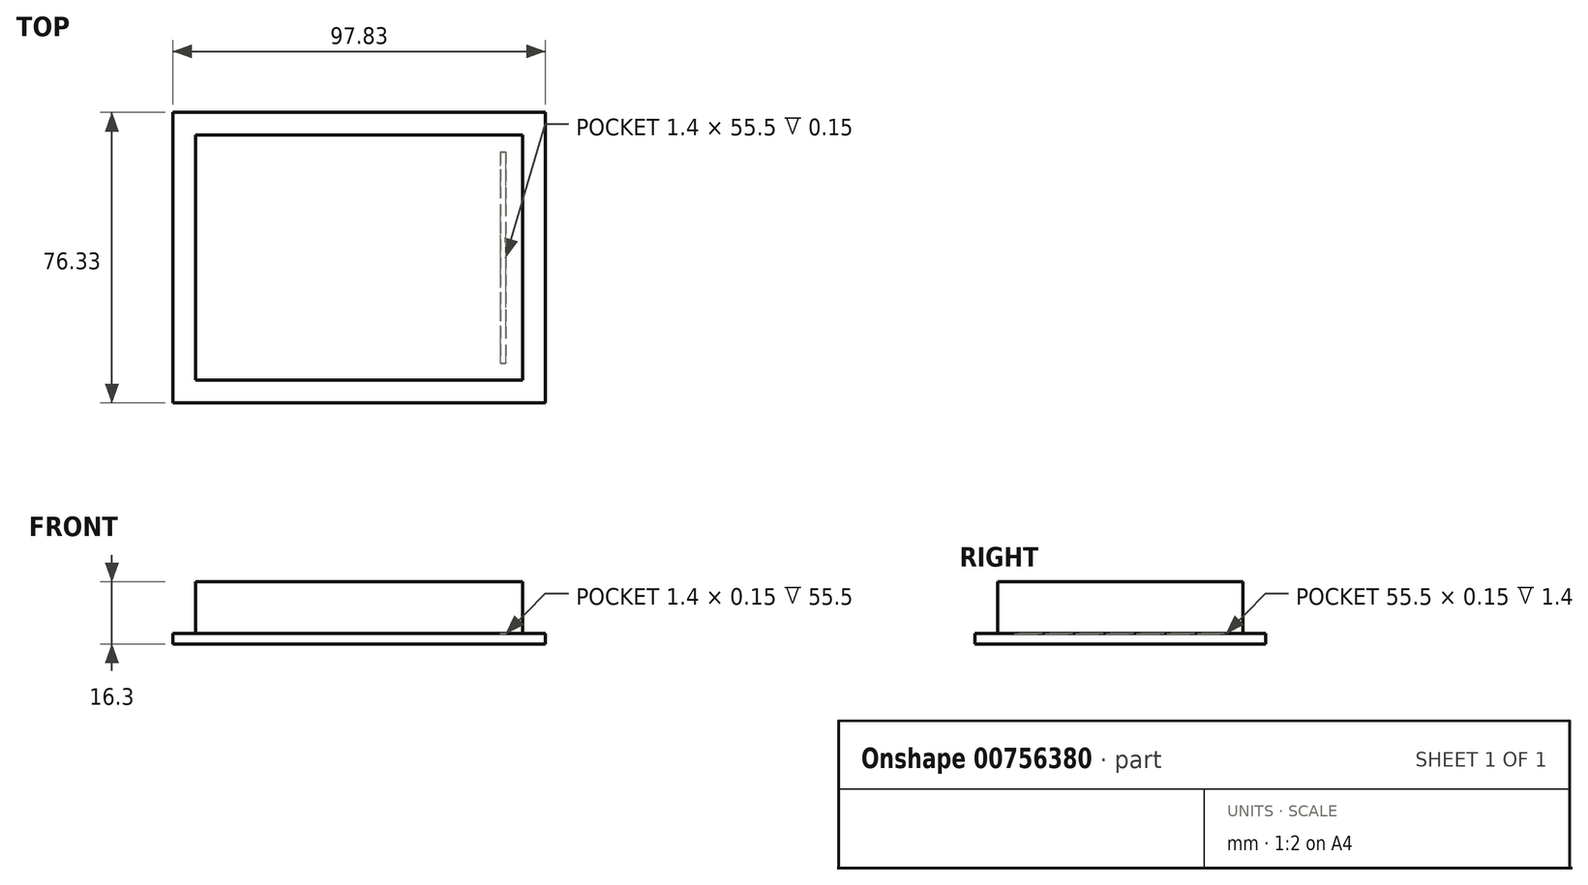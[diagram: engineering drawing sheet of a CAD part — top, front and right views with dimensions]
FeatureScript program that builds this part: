
annotation { "Feature Type Name" : "Feature", "Feature Type Description" : "" }
export const myFeature = defineFeature(function(context is Context, id is Id, definition is map)
    precondition{}
    {
        {
            var Q0;
            Q0=qCreatedBy(makeId("Top.planeOp"),FACE);
            var sketch = newSketch(context, id + "F0", { "sketchPlane" : qUnion([Q0])});
            skLineSegment(sketch, "E0.bottom", {"start": v(-42.32, 20.95) * mm, "end": v(34.68, 20.95) * mm});
            skLineSegment(sketch, "E0.top", {"start": v(-42.32, -34.55) * mm, "end": v(34.68, -34.55) * mm});
            skLineSegment(sketch, "E0.left", {"start": v(-42.32, 20.95) * mm, "end": v(-42.32, -34.55) * mm});
            skLineSegment(sketch, "E0.right", {"start": v(34.68, 20.95) * mm, "end": v(34.68, -34.55) * mm});
            skLineSegment(sketch, "E1", {"start": v(33.28, 20.95) * mm, "end": v(33.28, -34.55) * mm});
            skLineSegment(sketch, "E2.0", {"start": v(-52.74, 31.36) * mm, "end": v(45.09, 31.36) * mm});
            skLineSegment(sketch, "E2.1", {"start": v(-52.74, 31.36) * mm, "end": v(-52.74, -44.97) * mm});
            skLineSegment(sketch, "E2.2", {"start": v(-52.74, -44.97) * mm, "end": v(45.09, -44.97) * mm});
            skLineSegment(sketch, "E2.3", {"start": v(45.09, 31.36) * mm, "end": v(45.09, -44.97) * mm});
            skSolve(sketch);
        }
        {
            var Q0;
            {var subQ0=sQuery(id+"F0.wireOp",EDGE,"E0.right");Q0=makeQuery(id+"F0.imprint","IMPRINT",FACE,{"disambiguationData":[TD([[makeQuery(id+"F0.imprint","IMPRINT",EDGE,{"derivedFrom":subQ0}),-1.0]])]});}
            var Q1;
            {var subQ0=sQuery(id+"F0.wireOp",EDGE,"E0.left");Q1=makeQuery(id+"F0.imprint","IMPRINT",FACE,{"disambiguationData":[TD([[makeQuery(id+"F0.imprint","IMPRINT",EDGE,{"derivedFrom":subQ0}),1.0]])]});}
            extrude(context, id + "F1", {"entities" : qUnion([Q0, Q1]), "depth" : 2.6 * mm, "offsetDistance" : 25.4 * mm});
        }
        {
            var Q0;
            {var subQ0=sQuery(id+"F0.wireOp",EDGE,"E0.left");Q0=makeQuery(id+"F0.imprint","IMPRINT",FACE,{"disambiguationData":[TD([[makeQuery(id+"F0.imprint","IMPRINT",EDGE,{"derivedFrom":subQ0}),1.0]])]});}
            extrude(context, id + "F2", {"entities" : qUnion([Q0]), "operationType" : NewBodyOperationType.ADD, "depth" : 16.3 * mm, "offsetDistance" : 25.4 * mm});
        }
        {
            var Q0;
            {var subQ4=sQuery(id+"F0.wireOp",EDGE,"E0.left");Q0=makeQuery(id+"F0.imprint","IMPRINT",FACE,{"disambiguationData":[TD([[makeQuery(id+"F0.imprint","IMPRINT",EDGE,{"derivedFrom":subQ4}),-1.0]])]});}
            extrude(context, id + "F3", {"entities" : qUnion([Q0]), "depth" : 2.75 * mm, "offsetDistance" : 25.4 * mm});
        }
        {
            var Q0;
            {var subQ0=sQuery(id+"F0.wireOp",EDGE,"E0.right");Q0=makeQuery(id+"F0.imprint","IMPRINT",FACE,{"disambiguationData":[TD([[makeQuery(id+"F0.imprint","IMPRINT",EDGE,{"derivedFrom":subQ0}),-1.0]])]});}
            cPlane(context, id + "F4", {"entities" : qUnion([Q0]), "cplaneType" : CPlaneType.OFFSET, "offset" : 2.75 * mm, "width" : 152.4 * mm, "height" : 152.4 * mm});
        }
        {
            var Q0;
            Q0=qCreatedBy(id+"F4.planeOp",FACE);
            var sketch = newSketch(context, id + "F5", { "sketchPlane" : qUnion([Q0])});
            skLineSegment(sketch, "E3.bottom", {"start": v(-42.32, 20.95) * mm, "end": v(34.68, 20.95) * mm});
            skLineSegment(sketch, "E3.top", {"start": v(-42.32, -34.55) * mm, "end": v(34.68, -34.55) * mm});
            skLineSegment(sketch, "E3.left", {"start": v(-42.32, 20.95) * mm, "end": v(-42.32, -34.55) * mm});
            skLineSegment(sketch, "E3.right", {"start": v(34.68, 20.95) * mm, "end": v(34.68, -34.55) * mm});
            skLineSegment(sketch, "E4", {"start": v(33.28, 20.95) * mm, "end": v(33.28, -34.55) * mm});
            skLineSegment(sketch, "E5.0", {"start": v(-52.74, 31.36) * mm, "end": v(45.09, 31.36) * mm});
            skLineSegment(sketch, "E5.1", {"start": v(-52.74, 31.36) * mm, "end": v(-52.74, -44.97) * mm});
            skLineSegment(sketch, "E5.2", {"start": v(-52.74, -44.97) * mm, "end": v(45.09, -44.97) * mm});
            skLineSegment(sketch, "E5.3", {"start": v(45.09, 31.36) * mm, "end": v(45.09, -44.97) * mm});
            skLineSegment(sketch, "E6.0", {"start": v(-46.76, 25.39) * mm, "end": v(39.11, 25.39) * mm});
            skLineSegment(sketch, "E6.1", {"start": v(-46.76, 25.39) * mm, "end": v(-46.76, -39) * mm});
            skLineSegment(sketch, "E6.2", {"start": v(-46.76, -39) * mm, "end": v(39.11, -39) * mm});
            skLineSegment(sketch, "E6.3", {"start": v(39.11, 25.39) * mm, "end": v(39.11, -39) * mm});
            skSolve(sketch);
        }
        {
            var Q0;
            {var subQ0=sQuery(id+"F5.wireOp",EDGE,"E3.right");Q0=makeQuery(id+"F5.imprint","IMPRINT",FACE,{"disambiguationData":[TD([[makeQuery(id+"F5.imprint","IMPRINT",EDGE,{"derivedFrom":subQ0}),-1.0]])]});}
            extrude(context, id + "F6", {"entities" : qUnion([Q0]), "depth" : 13.55 * mm, "offsetDistance" : 25.4 * mm});
        }
        {
            var Q0;
            {var subQ4=sQuery(id+"F5.wireOp",EDGE,"E3.left");Q0=makeQuery(id+"F5.imprint","IMPRINT",FACE,{"disambiguationData":[TD([[makeQuery(id+"F5.imprint","IMPRINT",EDGE,{"derivedFrom":subQ4}),-1.0]])]});}
            extrude(context, id + "F7", {"entities" : qUnion([Q0]), "operationType" : NewBodyOperationType.ADD, "depth" : 13.55 * mm, "offsetDistance" : 25.4 * mm});
        }
    });
